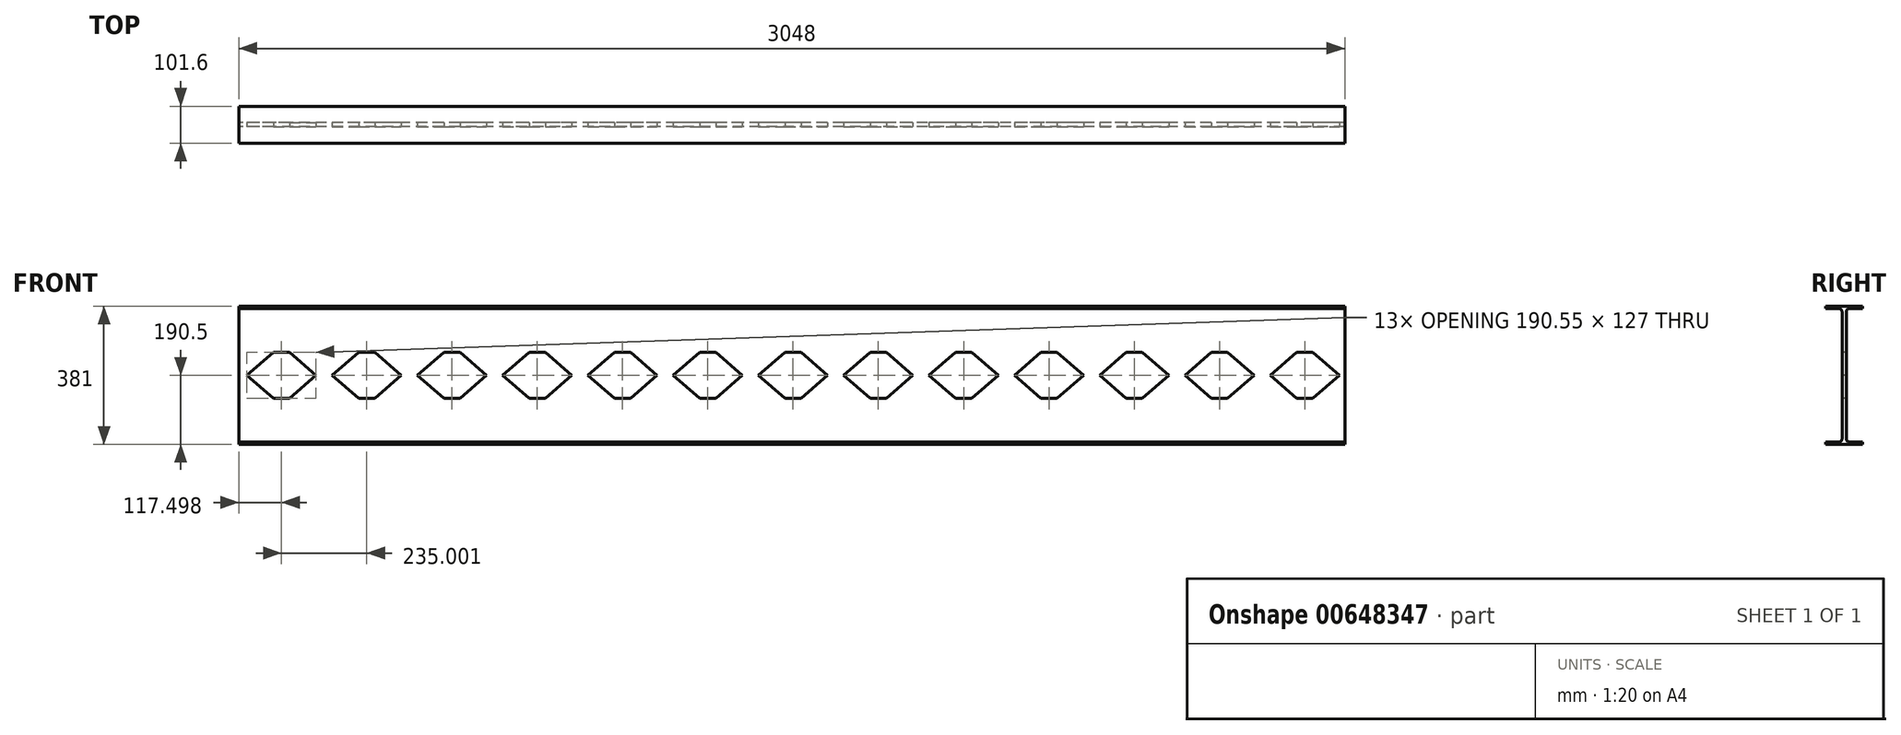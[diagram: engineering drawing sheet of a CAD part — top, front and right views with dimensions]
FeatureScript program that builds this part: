
annotation { "Feature Type Name" : "Feature", "Feature Type Description" : "" }
export const myFeature = defineFeature(function(context is Context, id is Id, definition is map)
    precondition{}
    {
        {
            var Q0;
            Q0=qCreatedBy(makeId("Right.planeOp"),FACE);
            var sketch = newSketch(context, id + "F0", { "sketchPlane" : qUnion([Q0])});
            skLineSegment(sketch, "E0", {"start": v(-5.84, 0) * mm, "end": v(-5.84, 175.73) * mm});
            skLineSegment(sketch, "E1", {"start": v(-13.78, 183.67) * mm, "end": v(-50.8, 183.67) * mm});
            skLineSegment(sketch, "E2", {"start": v(-50.8, 183.67) * mm, "end": v(-50.8, 190.5) * mm});
            skLineSegment(sketch, "E3", {"start": v(-50.8, 190.5) * mm, "end": v(0, 190.5) * mm});
            skPoint(sketch, "E4.visualSharp", {"position": v(-5.84, 183.67) * mm});
            skArc(sketch, "E4.filletArc", {"start": v(-5.84, 175.73) * mm, "mid": v(-8.17, 181.34) * mm, "end": v(-13.78, 183.67) * mm});
            skLineSegment(sketch, "E5.MirrorCS", {"start": v(5.84, 0) * mm, "end": v(5.84, 175.73) * mm});
            skPoint(sketch, "E6.MirrorP", {"position": v(5.84, 183.67) * mm});
            skLineSegment(sketch, "E7.MirrorCS", {"start": v(13.78, 183.67) * mm, "end": v(50.8, 183.67) * mm});
            skArc(sketch, "E8.MirrorCS", {"start": v(5.84, 175.73) * mm, "mid": v(8.17, 181.34) * mm, "end": v(13.78, 183.67) * mm});
            skLineSegment(sketch, "E9.MirrorCS", {"start": v(50.8, 190.5) * mm, "end": v(0, 190.5) * mm});
            skLineSegment(sketch, "E10.MirrorCS", {"start": v(50.8, 183.67) * mm, "end": v(50.8, 190.5) * mm});
            skLineSegment(sketch, "E11.MirrorCS", {"start": v(50.8, -183.67) * mm, "end": v(50.8, -190.5) * mm});
            skLineSegment(sketch, "E12.MirrorCS", {"start": v(-50.8, -183.67) * mm, "end": v(-50.8, -190.5) * mm});
            skArc(sketch, "E13.MirrorCS", {"start": v(5.84, -175.73) * mm, "mid": v(8.17, -181.34) * mm, "end": v(13.78, -183.67) * mm});
            skArc(sketch, "E14.MirrorCS", {"start": v(-5.84, -175.73) * mm, "mid": v(-8.17, -181.34) * mm, "end": v(-13.78, -183.67) * mm});
            skLineSegment(sketch, "E15.MirrorCS", {"start": v(-5.84, 0) * mm, "end": v(-5.84, -175.73) * mm});
            skPoint(sketch, "E16.MirrorP", {"position": v(5.84, -183.67) * mm});
            skLineSegment(sketch, "E17.MirrorCS", {"start": v(-13.78, -183.67) * mm, "end": v(-50.8, -183.67) * mm});
            skPoint(sketch, "E18.MirrorP", {"position": v(-5.84, -183.67) * mm});
            skLineSegment(sketch, "E19.MirrorCS", {"start": v(-50.8, -190.5) * mm, "end": v(0, -190.5) * mm});
            skLineSegment(sketch, "E20.MirrorCS", {"start": v(13.78, -183.67) * mm, "end": v(50.8, -183.67) * mm});
            skLineSegment(sketch, "E21.MirrorCS", {"start": v(50.8, -190.5) * mm, "end": v(0, -190.5) * mm});
            skLineSegment(sketch, "E22.MirrorCS", {"start": v(5.84, 0) * mm, "end": v(5.84, -175.73) * mm});
            skSolve(sketch);
        }
        {
            var Q0;
            Q0=makeQuery(id+"F0.imprint","IMPRINT",FACE,{"disambiguationData":[TD([[makeQuery(id+"F0.imprint","IMPRINT",EDGE,{"derivedFrom":sQuery(id+"F0.wireOp",EDGE,"E0")}),-1.0]])]});
            extrude(context, id + "F1", {"entities" : qUnion([Q0]), "depth" : 3048 * mm, "offsetDistance" : 25.4 * mm});
        }
        {
            var Q0;
            Q0=makeQuery(id+"F1.opExtrude","SWEPT_FACE",FACE,{"disambiguationData":[OSD([sQuery(id+"F0.wireOp",EDGE,"E0"),sQuery(id+"F0.wireOp",EDGE,"E15.MirrorCS")])]});
            var sketch = newSketch(context, id + "F2", { "sketchPlane" : qUnion([Q0])});
            skLineSegment(sketch, "E23", {"start": v(22.23, 0) * mm, "end": v(95.27, 63.5) * mm});
            skLineSegment(sketch, "E24", {"start": v(95.27, 63.5) * mm, "end": v(139.72, 63.5) * mm});
            skLineSegment(sketch, "E25", {"start": v(139.72, 63.5) * mm, "end": v(212.77, 0) * mm});
            skLineSegment(sketch, "E26", {"start": v(212.77, 0) * mm, "end": v(139.72, -63.5) * mm});
            skLineSegment(sketch, "E27", {"start": v(139.72, -63.5) * mm, "end": v(95.27, -63.5) * mm});
            skLineSegment(sketch, "E28", {"start": v(95.27, -63.5) * mm, "end": v(22.23, 0) * mm});
            skLineSegment(sketch, "E29", {"start": v(0, 0) * mm, "end": v(212.77, 0) * mm, "construction": true});
            skLineSegment(sketch, "E30.1.0.0", {"start": v(330.27, 63.5) * mm, "end": v(374.72, 63.5) * mm});
            skLineSegment(sketch, "E30.1.0.1", {"start": v(257.23, 0) * mm, "end": v(330.27, 63.5) * mm});
            skLineSegment(sketch, "E30.1.0.2", {"start": v(374.72, 63.5) * mm, "end": v(447.77, 0) * mm});
            skLineSegment(sketch, "E30.1.0.3", {"start": v(447.77, 0) * mm, "end": v(374.72, -63.5) * mm});
            skLineSegment(sketch, "E30.1.0.4", {"start": v(374.72, -63.5) * mm, "end": v(330.27, -63.5) * mm});
            skLineSegment(sketch, "E30.1.0.5", {"start": v(330.27, -63.5) * mm, "end": v(257.23, 0) * mm});
            skLineSegment(sketch, "E30.2.0.0", {"start": v(565.27, 63.5) * mm, "end": v(609.72, 63.5) * mm});
            skLineSegment(sketch, "E30.2.0.1", {"start": v(492.23, 0) * mm, "end": v(565.27, 63.5) * mm});
            skLineSegment(sketch, "E30.2.0.2", {"start": v(609.72, 63.5) * mm, "end": v(682.77, 0) * mm});
            skLineSegment(sketch, "E30.2.0.3", {"start": v(682.77, 0) * mm, "end": v(609.72, -63.5) * mm});
            skLineSegment(sketch, "E30.2.0.4", {"start": v(609.72, -63.5) * mm, "end": v(565.27, -63.5) * mm});
            skLineSegment(sketch, "E30.2.0.5", {"start": v(565.27, -63.5) * mm, "end": v(492.23, 0) * mm});
            skLineSegment(sketch, "E30.3.0.0", {"start": v(800.28, 63.5) * mm, "end": v(844.73, 63.5) * mm});
            skLineSegment(sketch, "E30.3.0.1", {"start": v(727.23, 0) * mm, "end": v(800.28, 63.5) * mm});
            skLineSegment(sketch, "E30.3.0.2", {"start": v(844.73, 63.5) * mm, "end": v(917.77, 0) * mm});
            skLineSegment(sketch, "E30.3.0.3", {"start": v(917.77, 0) * mm, "end": v(844.73, -63.5) * mm});
            skLineSegment(sketch, "E30.3.0.4", {"start": v(844.73, -63.5) * mm, "end": v(800.28, -63.5) * mm});
            skLineSegment(sketch, "E30.3.0.5", {"start": v(800.28, -63.5) * mm, "end": v(727.23, 0) * mm});
            skLineSegment(sketch, "E30.4.0.0", {"start": v(1035.28, 63.5) * mm, "end": v(1079.73, 63.5) * mm});
            skLineSegment(sketch, "E30.4.0.1", {"start": v(962.23, 0) * mm, "end": v(1035.28, 63.5) * mm});
            skLineSegment(sketch, "E30.4.0.2", {"start": v(1079.73, 63.5) * mm, "end": v(1152.77, 0) * mm});
            skLineSegment(sketch, "E30.4.0.3", {"start": v(1152.77, 0) * mm, "end": v(1079.73, -63.5) * mm});
            skLineSegment(sketch, "E30.4.0.4", {"start": v(1079.73, -63.5) * mm, "end": v(1035.28, -63.5) * mm});
            skLineSegment(sketch, "E30.4.0.5", {"start": v(1035.28, -63.5) * mm, "end": v(962.23, 0) * mm});
            skLineSegment(sketch, "E30.5.0.0", {"start": v(1270.28, 63.5) * mm, "end": v(1314.73, 63.5) * mm});
            skLineSegment(sketch, "E30.5.0.1", {"start": v(1197.23, 0) * mm, "end": v(1270.28, 63.5) * mm});
            skLineSegment(sketch, "E30.5.0.2", {"start": v(1314.73, 63.5) * mm, "end": v(1387.78, 0) * mm});
            skLineSegment(sketch, "E30.5.0.3", {"start": v(1387.78, 0) * mm, "end": v(1314.73, -63.5) * mm});
            skLineSegment(sketch, "E30.5.0.4", {"start": v(1314.73, -63.5) * mm, "end": v(1270.28, -63.5) * mm});
            skLineSegment(sketch, "E30.5.0.5", {"start": v(1270.28, -63.5) * mm, "end": v(1197.23, 0) * mm});
            skLineSegment(sketch, "E30.6.0.0", {"start": v(1505.28, 63.5) * mm, "end": v(1549.73, 63.5) * mm});
            skLineSegment(sketch, "E30.6.0.1", {"start": v(1432.23, 0) * mm, "end": v(1505.28, 63.5) * mm});
            skLineSegment(sketch, "E30.6.0.2", {"start": v(1549.73, 63.5) * mm, "end": v(1622.78, 0) * mm});
            skLineSegment(sketch, "E30.6.0.3", {"start": v(1622.78, 0) * mm, "end": v(1549.73, -63.5) * mm});
            skLineSegment(sketch, "E30.6.0.4", {"start": v(1549.73, -63.5) * mm, "end": v(1505.28, -63.5) * mm});
            skLineSegment(sketch, "E30.6.0.5", {"start": v(1505.28, -63.5) * mm, "end": v(1432.23, 0) * mm});
            skLineSegment(sketch, "E30.7.0.0", {"start": v(1740.28, 63.5) * mm, "end": v(1784.73, 63.5) * mm});
            skLineSegment(sketch, "E30.7.0.1", {"start": v(1667.23, 0) * mm, "end": v(1740.28, 63.5) * mm});
            skLineSegment(sketch, "E30.7.0.2", {"start": v(1784.73, 63.5) * mm, "end": v(1857.78, 0) * mm});
            skLineSegment(sketch, "E30.7.0.3", {"start": v(1857.78, 0) * mm, "end": v(1784.73, -63.5) * mm});
            skLineSegment(sketch, "E30.7.0.4", {"start": v(1784.73, -63.5) * mm, "end": v(1740.28, -63.5) * mm});
            skLineSegment(sketch, "E30.7.0.5", {"start": v(1740.28, -63.5) * mm, "end": v(1667.23, 0) * mm});
            skLineSegment(sketch, "E30.8.0.0", {"start": v(1975.28, 63.5) * mm, "end": v(2019.73, 63.5) * mm});
            skLineSegment(sketch, "E30.8.0.1", {"start": v(1902.23, 0) * mm, "end": v(1975.28, 63.5) * mm});
            skLineSegment(sketch, "E30.8.0.2", {"start": v(2019.73, 63.5) * mm, "end": v(2092.78, 0) * mm});
            skLineSegment(sketch, "E30.8.0.3", {"start": v(2092.78, 0) * mm, "end": v(2019.73, -63.5) * mm});
            skLineSegment(sketch, "E30.8.0.4", {"start": v(2019.73, -63.5) * mm, "end": v(1975.28, -63.5) * mm});
            skLineSegment(sketch, "E30.8.0.5", {"start": v(1975.28, -63.5) * mm, "end": v(1902.23, 0) * mm});
            skLineSegment(sketch, "E30.9.0.0", {"start": v(2210.28, 63.5) * mm, "end": v(2254.73, 63.5) * mm});
            skLineSegment(sketch, "E30.9.0.1", {"start": v(2137.23, 0) * mm, "end": v(2210.28, 63.5) * mm});
            skLineSegment(sketch, "E30.9.0.2", {"start": v(2254.73, 63.5) * mm, "end": v(2327.78, 0) * mm});
            skLineSegment(sketch, "E30.9.0.3", {"start": v(2327.78, 0) * mm, "end": v(2254.73, -63.5) * mm});
            skLineSegment(sketch, "E30.9.0.4", {"start": v(2254.73, -63.5) * mm, "end": v(2210.28, -63.5) * mm});
            skLineSegment(sketch, "E30.9.0.5", {"start": v(2210.28, -63.5) * mm, "end": v(2137.23, 0) * mm});
            skLineSegment(sketch, "E30.10.0.0", {"start": v(2445.28, 63.5) * mm, "end": v(2489.73, 63.5) * mm});
            skLineSegment(sketch, "E30.10.0.1", {"start": v(2372.23, 0) * mm, "end": v(2445.28, 63.5) * mm});
            skLineSegment(sketch, "E30.10.0.2", {"start": v(2489.73, 63.5) * mm, "end": v(2562.78, 0) * mm});
            skLineSegment(sketch, "E30.10.0.3", {"start": v(2562.78, 0) * mm, "end": v(2489.73, -63.5) * mm});
            skLineSegment(sketch, "E30.10.0.4", {"start": v(2489.73, -63.5) * mm, "end": v(2445.28, -63.5) * mm});
            skLineSegment(sketch, "E30.10.0.5", {"start": v(2445.28, -63.5) * mm, "end": v(2372.23, 0) * mm});
            skLineSegment(sketch, "E30.11.0.0", {"start": v(2680.28, 63.5) * mm, "end": v(2724.73, 63.5) * mm});
            skLineSegment(sketch, "E30.11.0.1", {"start": v(2607.23, 0) * mm, "end": v(2680.28, 63.5) * mm});
            skLineSegment(sketch, "E30.11.0.2", {"start": v(2724.73, 63.5) * mm, "end": v(2797.78, 0) * mm});
            skLineSegment(sketch, "E30.11.0.3", {"start": v(2797.78, 0) * mm, "end": v(2724.73, -63.5) * mm});
            skLineSegment(sketch, "E30.11.0.4", {"start": v(2724.73, -63.5) * mm, "end": v(2680.28, -63.5) * mm});
            skLineSegment(sketch, "E30.11.0.5", {"start": v(2680.28, -63.5) * mm, "end": v(2607.23, 0) * mm});
            skLineSegment(sketch, "E30.12.0.0", {"start": v(2915.28, 63.5) * mm, "end": v(2959.73, 63.5) * mm});
            skLineSegment(sketch, "E30.12.0.1", {"start": v(2842.23, 0) * mm, "end": v(2915.28, 63.5) * mm});
            skLineSegment(sketch, "E30.12.0.2", {"start": v(2959.73, 63.5) * mm, "end": v(3032.78, 0) * mm});
            skLineSegment(sketch, "E30.12.0.3", {"start": v(3032.78, 0) * mm, "end": v(2959.73, -63.5) * mm});
            skLineSegment(sketch, "E30.12.0.4", {"start": v(2959.73, -63.5) * mm, "end": v(2915.28, -63.5) * mm});
            skLineSegment(sketch, "E30.12.0.5", {"start": v(2915.28, -63.5) * mm, "end": v(2842.23, 0) * mm});
            skLineSegment(sketch, "E30.direction1", {"start": v(95.27, 63.5) * mm, "end": v(330.27, 63.5) * mm, "construction": true});
            skSolve(sketch);
        }
        {
            var Q0;
            Q0=makeQuery(id+"F2.imprint","IMPRINT",FACE,{"disambiguationData":[TD([[makeQuery(id+"F2.imprint","IMPRINT",EDGE,{"derivedFrom":sQuery(id+"F2.wireOp",EDGE,"E23")}),-1.0]])]});
            var Q1;
            Q1=makeQuery(id+"F2.imprint","IMPRINT",FACE,{"disambiguationData":[TD([[makeQuery(id+"F2.imprint","IMPRINT",EDGE,{"derivedFrom":sQuery(id+"F2.wireOp",EDGE,"E30.1.0.0")}),-1.0]])]});
            var Q2;
            Q2=makeQuery(id+"F2.imprint","IMPRINT",FACE,{"disambiguationData":[TD([[makeQuery(id+"F2.imprint","IMPRINT",EDGE,{"derivedFrom":sQuery(id+"F2.wireOp",EDGE,"E30.2.0.0")}),-1.0]])]});
            var Q3;
            Q3=makeQuery(id+"F2.imprint","IMPRINT",FACE,{"disambiguationData":[TD([[makeQuery(id+"F2.imprint","IMPRINT",EDGE,{"derivedFrom":sQuery(id+"F2.wireOp",EDGE,"E30.3.0.0")}),-1.0]])]});
            var Q4;
            Q4=makeQuery(id+"F2.imprint","IMPRINT",FACE,{"disambiguationData":[TD([[makeQuery(id+"F2.imprint","IMPRINT",EDGE,{"derivedFrom":sQuery(id+"F2.wireOp",EDGE,"E30.4.0.0")}),-1.0]])]});
            var Q5;
            Q5=makeQuery(id+"F2.imprint","IMPRINT",FACE,{"disambiguationData":[TD([[makeQuery(id+"F2.imprint","IMPRINT",EDGE,{"derivedFrom":sQuery(id+"F2.wireOp",EDGE,"E30.5.0.0")}),-1.0]])]});
            var Q6;
            Q6=makeQuery(id+"F2.imprint","IMPRINT",FACE,{"disambiguationData":[TD([[makeQuery(id+"F2.imprint","IMPRINT",EDGE,{"derivedFrom":sQuery(id+"F2.wireOp",EDGE,"E30.6.0.0")}),-1.0]])]});
            var Q7;
            Q7=makeQuery(id+"F2.imprint","IMPRINT",FACE,{"disambiguationData":[TD([[makeQuery(id+"F2.imprint","IMPRINT",EDGE,{"derivedFrom":sQuery(id+"F2.wireOp",EDGE,"E30.7.0.0")}),-1.0]])]});
            var Q8;
            Q8=makeQuery(id+"F2.imprint","IMPRINT",FACE,{"disambiguationData":[TD([[makeQuery(id+"F2.imprint","IMPRINT",EDGE,{"derivedFrom":sQuery(id+"F2.wireOp",EDGE,"E30.8.0.0")}),-1.0]])]});
            var Q9;
            Q9=makeQuery(id+"F2.imprint","IMPRINT",FACE,{"disambiguationData":[TD([[makeQuery(id+"F2.imprint","IMPRINT",EDGE,{"derivedFrom":sQuery(id+"F2.wireOp",EDGE,"E30.9.0.0")}),-1.0]])]});
            var Q10;
            Q10=makeQuery(id+"F2.imprint","IMPRINT",FACE,{"disambiguationData":[TD([[makeQuery(id+"F2.imprint","IMPRINT",EDGE,{"derivedFrom":sQuery(id+"F2.wireOp",EDGE,"E30.10.0.0")}),-1.0]])]});
            var Q11;
            Q11=makeQuery(id+"F2.imprint","IMPRINT",FACE,{"disambiguationData":[TD([[makeQuery(id+"F2.imprint","IMPRINT",EDGE,{"derivedFrom":sQuery(id+"F2.wireOp",EDGE,"E30.11.0.0")}),-1.0]])]});
            var Q12;
            Q12=makeQuery(id+"F2.imprint","IMPRINT",FACE,{"disambiguationData":[TD([[makeQuery(id+"F2.imprint","IMPRINT",EDGE,{"derivedFrom":sQuery(id+"F2.wireOp",EDGE,"E30.12.0.0")}),-1.0]])]});
            extrude(context, id + "F3", {"entities" : qUnion([Q0, Q1, Q2, Q3, Q4, Q5, Q6, Q7, Q8, Q9, Q10, Q11, Q12]), "operationType" : NewBodyOperationType.REMOVE, "endBound" : BoundingType.THROUGH_ALL, "oppositeDirection" : true, "depth" : 25.4 * mm, "offsetDistance" : 25.4 * mm});
        }
    });
